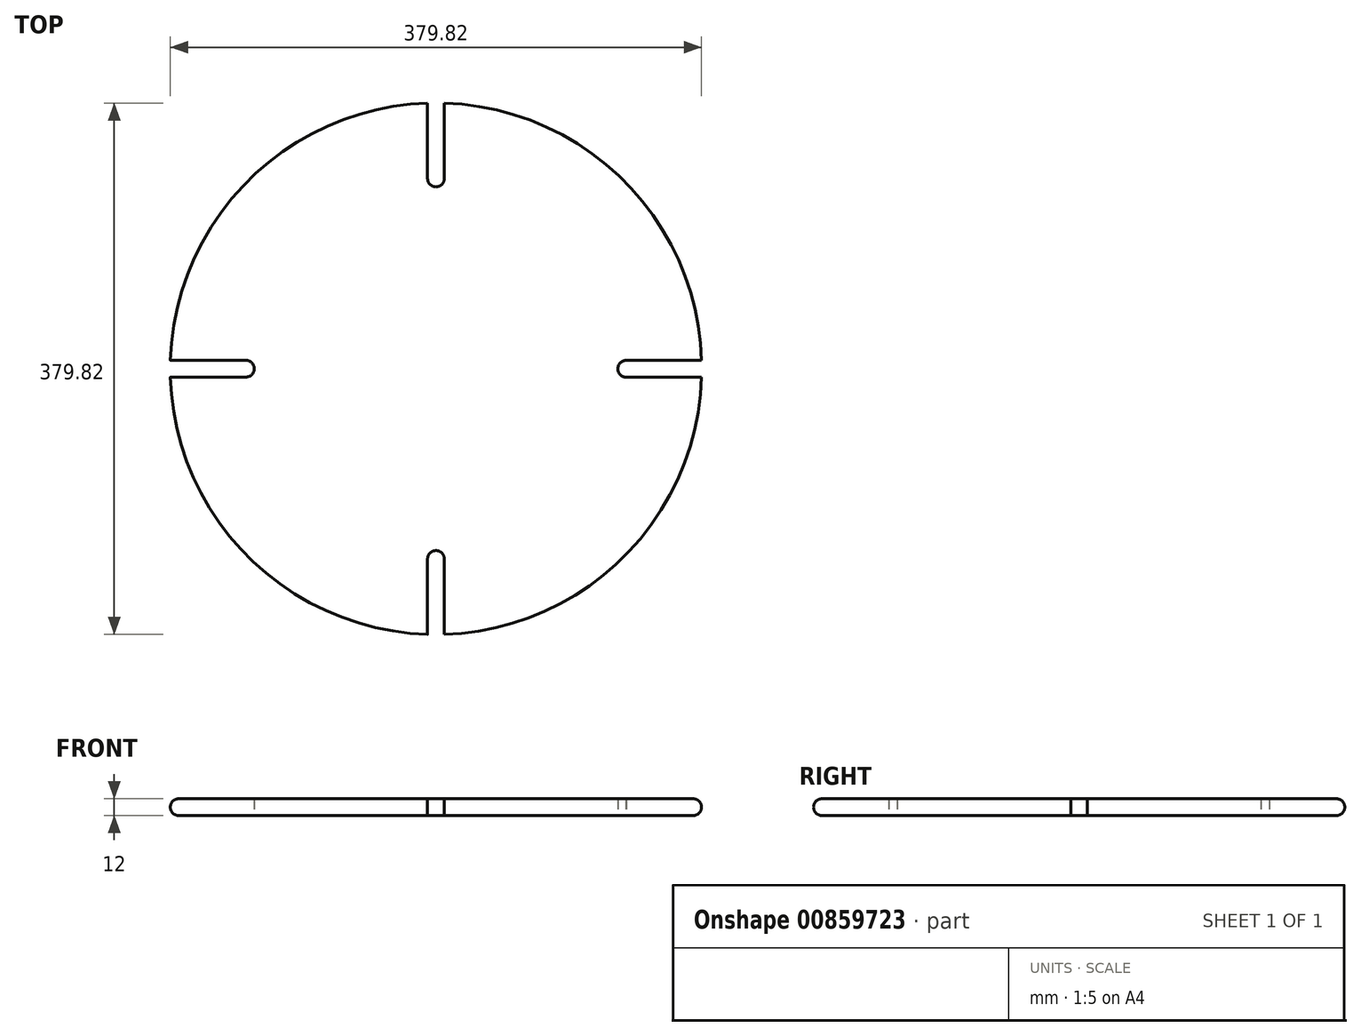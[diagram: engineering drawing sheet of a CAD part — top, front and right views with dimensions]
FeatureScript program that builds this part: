
annotation { "Feature Type Name" : "Feature", "Feature Type Description" : "" }
export const myFeature = defineFeature(function(context is Context, id is Id, definition is map)
    precondition{}
    {
        {
            var Q0;
            Q0=qCreatedBy(makeId("Top.planeOp"),FACE);
            var sketch = newSketch(context, id + "F0", { "sketchPlane" : qUnion([Q0])});
            skArc(sketch, "E0", {"start": v(-6, 189.9) * mm, "mid": v(-134.35, 134.35) * mm, "end": v(-189.9, 6) * mm});
            skArc(sketch, "E1", {"start": v(-6, 136.13) * mm, "mid": v(0, 130) * mm, "end": v(6, 136.13) * mm});
            skArc(sketch, "E2", {"start": v(135.87, 6) * mm, "mid": v(130, -0.13) * mm, "end": v(136.13, -6) * mm});
            skArc(sketch, "E3", {"start": v(6, -136.13) * mm, "mid": v(0, -130) * mm, "end": v(-6, -136.13) * mm});
            skArc(sketch, "E4", {"start": v(-136, -6) * mm, "mid": v(-130, 0) * mm, "end": v(-136, 6) * mm});
            skLineSegment(sketch, "E5", {"start": v(6, 135.87) * mm, "end": v(6, 189.9) * mm});
            skLineSegment(sketch, "E6", {"start": v(-6, 135.87) * mm, "end": v(-6, 189.9) * mm});
            skLineSegment(sketch, "E7", {"start": v(135.87, 6) * mm, "end": v(189.9, 6) * mm});
            skLineSegment(sketch, "E8", {"start": v(135.87, -6) * mm, "end": v(189.9, -6) * mm});
            skArc(sketch, "E9.trimOffspring", {"start": v(189.9, 6) * mm, "mid": v(134.35, 134.35) * mm, "end": v(6, 189.9) * mm});
            skLineSegment(sketch, "E10", {"start": v(-6, -135.87) * mm, "end": v(-6, -189.9) * mm});
            skLineSegment(sketch, "E11", {"start": v(6, -135.87) * mm, "end": v(6, -189.9) * mm});
            skArc(sketch, "E12.trimOffspring", {"start": v(6, -189.9) * mm, "mid": v(134.35, -134.35) * mm, "end": v(189.9, -6) * mm});
            skLineSegment(sketch, "E13", {"start": v(-136, 6) * mm, "end": v(-189.9, 6) * mm});
            skLineSegment(sketch, "E14", {"start": v(-136, -6) * mm, "end": v(-189.9, -6) * mm});
            skArc(sketch, "E15.trimOffspring", {"start": v(-189.9, -6) * mm, "mid": v(-134.35, -134.35) * mm, "end": v(-6, -189.9) * mm});
            skSolve(sketch);
        }
        {
            var Q0;
            {var subQ12=sQuery(id+"F0.wireOp",EDGE,"E0");Q0=makeQuery(id+"F0.imprint","IMPRINT",FACE,{"disambiguationData":[TD([[makeQuery(id+"F0.imprint","IMPRINT",EDGE,{"derivedFrom":subQ12}),1.0]])]});}
            extrude(context, id + "F1", {"entities" : qUnion([Q0]), "depth" : 12 * mm, "offsetDistance" : 25 * mm});
        }
        {
            var Q0;
            Q0=makeQuery(id+"F1.opExtrude","CAP_EDGE",EDGE,{"disambiguationData":[OSD([sQuery(id+"F0.wireOp",EDGE,"E15.trimOffspring")])],"isStart":false});
            var Q1;
            Q1=makeQuery(id+"F1.opExtrude","CAP_EDGE",EDGE,{"disambiguationData":[OSD([sQuery(id+"F0.wireOp",EDGE,"E15.trimOffspring")])],"isStart":true});
            var Q2;
            Q2=makeQuery(id+"F1.opExtrude","CAP_EDGE",EDGE,{"disambiguationData":[OSD([sQuery(id+"F0.wireOp",EDGE,"E12.trimOffspring")])],"isStart":false});
            var Q3;
            Q3=makeQuery(id+"F1.opExtrude","CAP_EDGE",EDGE,{"disambiguationData":[OSD([sQuery(id+"F0.wireOp",EDGE,"E12.trimOffspring")])],"isStart":true});
            var Q4;
            Q4=makeQuery(id+"F1.opExtrude","CAP_EDGE",EDGE,{"disambiguationData":[OSD([sQuery(id+"F0.wireOp",EDGE,"E0")])],"isStart":false});
            var Q5;
            Q5=makeQuery(id+"F1.opExtrude","CAP_EDGE",EDGE,{"disambiguationData":[OSD([sQuery(id+"F0.wireOp",EDGE,"E0")])],"isStart":true});
            var Q6;
            Q6=makeQuery(id+"F1.opExtrude","CAP_EDGE",EDGE,{"disambiguationData":[OSD([sQuery(id+"F0.wireOp",EDGE,"E9.trimOffspring")])],"isStart":false});
            var Q7;
            Q7=makeQuery(id+"F1.opExtrude","CAP_EDGE",EDGE,{"disambiguationData":[OSD([sQuery(id+"F0.wireOp",EDGE,"E9.trimOffspring")])],"isStart":true});
            fillet(context, id + "F2", {"entities" : qUnion([Q0, Q1, Q2, Q3, Q4, Q5, Q6, Q7]), "radius" : 6 * mm, "tangentPropagation" : true, "allowEdgeOverflow" : false});
        }
    });
